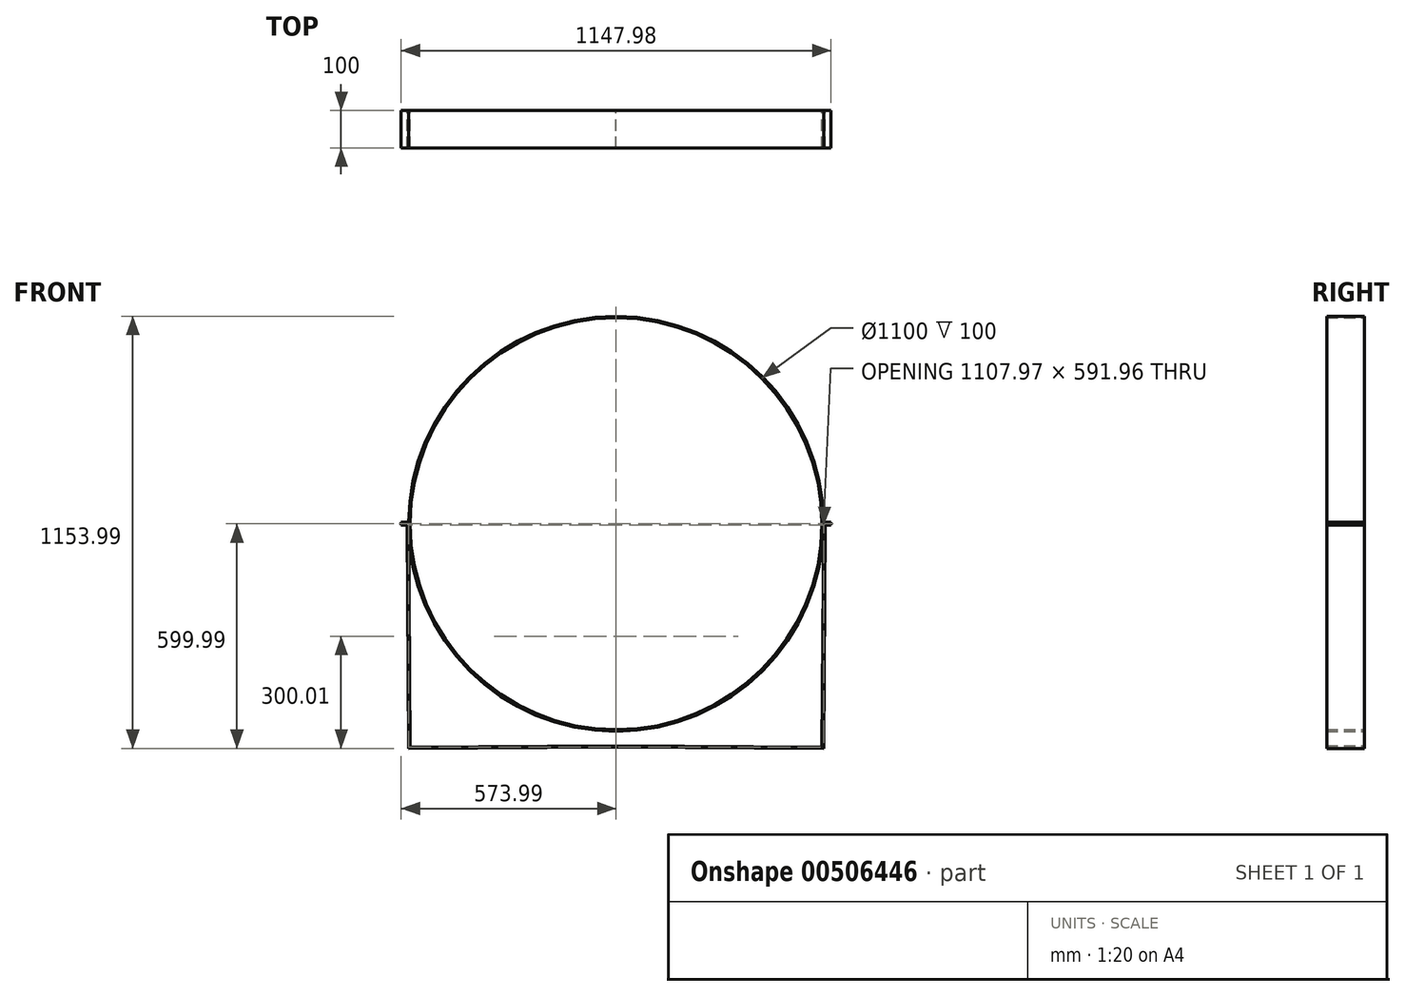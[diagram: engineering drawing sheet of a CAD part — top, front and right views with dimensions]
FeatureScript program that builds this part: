
annotation { "Feature Type Name" : "Feature", "Feature Type Description" : "" }
export const myFeature = defineFeature(function(context is Context, id is Id, definition is map)
    precondition{}
    {
        {
            var Q0;
            Q0=qCreatedBy(makeId("Front.planeOp"),FACE);
            var sketch = newSketch(context, id + "F0", { "sketchPlane" : qUnion([Q0])});
            skCircle(sketch, "E0", {"center": v(0, 0) * mm, "radius": 550 * mm});
            skCircle(sketch, "E1", {"center": v(0, 0) * mm, "radius": 554 * mm});
            skLineSegment(sketch, "E2", {"start": v(0, 0) * mm, "end": v(-690.21, 0) * mm, "construction": true});
            skLineSegment(sketch, "E3", {"start": v(-553.99, 4) * mm, "end": v(-573.99, 4) * mm});
            skLineSegment(sketch, "E4", {"start": v(-573.99, 4) * mm, "end": v(-573.99, 0) * mm});
            skLineSegment(sketch, "E5.MirrorCS", {"start": v(-553.99, -4) * mm, "end": v(-573.99, -4) * mm});
            skLineSegment(sketch, "E6.MirrorCS", {"start": v(-573.99, -4) * mm, "end": v(-573.99, 0) * mm});
            skLineSegment(sketch, "E7", {"start": v(0, 0) * mm, "end": v(0, 668.71) * mm, "construction": true});
            skLineSegment(sketch, "E8.MirrorCS", {"start": v(573.99, 4) * mm, "end": v(573.99, 0) * mm});
            skLineSegment(sketch, "E9.MirrorCS", {"start": v(573.99, -4) * mm, "end": v(573.99, 0) * mm});
            skLineSegment(sketch, "E10.MirrorCS", {"start": v(553.99, 4) * mm, "end": v(573.99, 4) * mm});
            skLineSegment(sketch, "E11.MirrorCS", {"start": v(553.99, -4) * mm, "end": v(573.99, -4) * mm});
            skLineSegment(sketch, "E12", {"start": v(-553.99, -4) * mm, "end": v(-557.99, -4) * mm});
            skLineSegment(sketch, "E13", {"start": v(-557.99, -4) * mm, "end": v(-553.99, -599.99) * mm});
            skLineSegment(sketch, "E14", {"start": v(-553.99, -4) * mm, "end": v(-550.01, -595.96) * mm});
            skLineSegment(sketch, "E15", {"start": v(-550.01, -595.96) * mm, "end": v(0, -592.27) * mm});
            skLineSegment(sketch, "E16", {"start": v(-553.99, -599.99) * mm, "end": v(0, -596.27) * mm});
            skLineSegment(sketch, "E17.MirrorCS", {"start": v(553.99, -4) * mm, "end": v(550.01, -595.96) * mm});
            skLineSegment(sketch, "E18.MirrorCS", {"start": v(557.99, -4) * mm, "end": v(553.99, -599.99) * mm});
            skLineSegment(sketch, "E19.MirrorCS", {"start": v(553.99, -599.99) * mm, "end": v(0, -596.27) * mm});
            skLineSegment(sketch, "E20.MirrorCS", {"start": v(550.01, -595.96) * mm, "end": v(0, -592.27) * mm});
            skSolve(sketch);
        }
        {
            var Q0;
            Q0=qSketchRegion(id+"F0",true);
            extrude(context, id + "F1", {"entities" : qUnion([Q0]), "depth" : 100 * mm});
        }
    });
